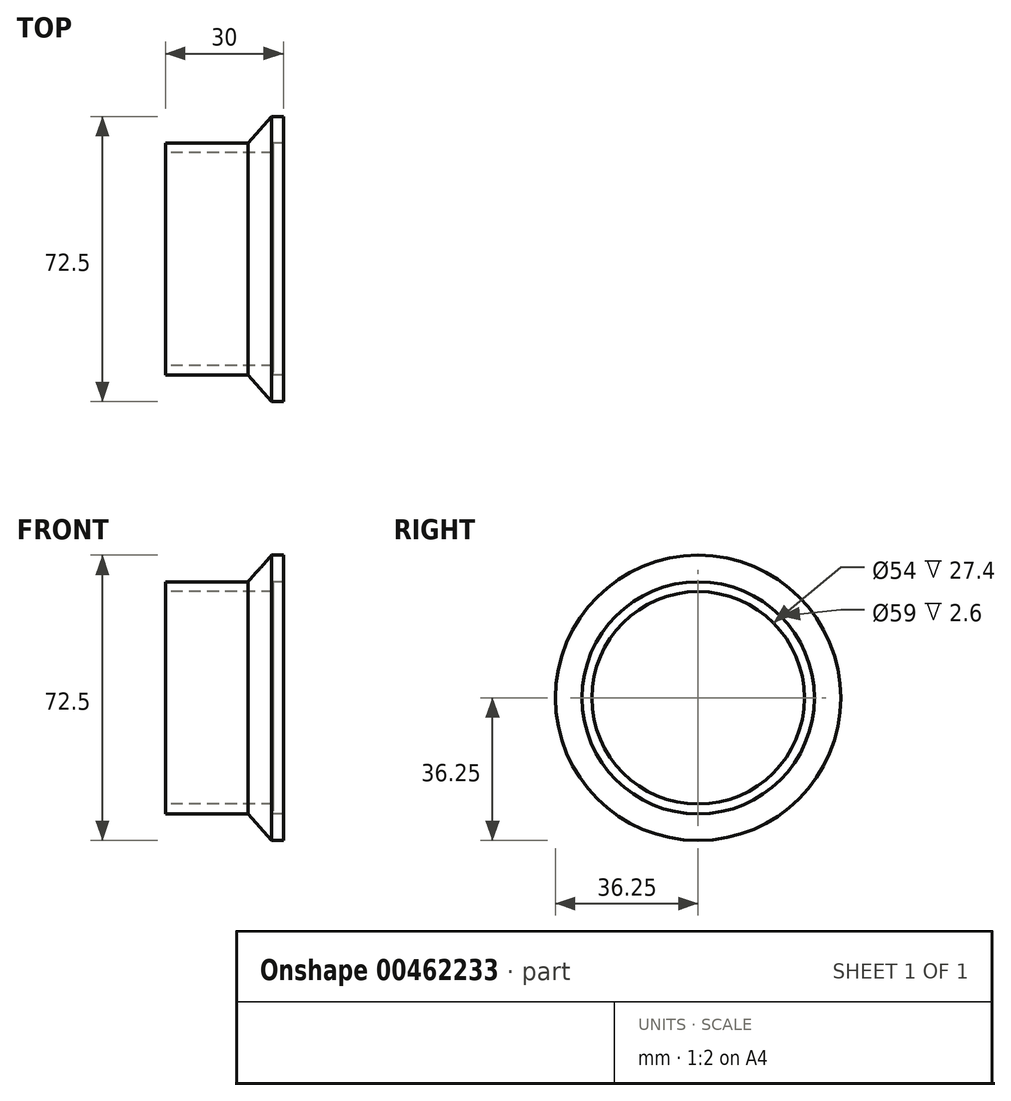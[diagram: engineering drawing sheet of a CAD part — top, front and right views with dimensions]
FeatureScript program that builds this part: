
annotation { "Feature Type Name" : "Feature", "Feature Type Description" : "" }
export const myFeature = defineFeature(function(context is Context, id is Id, definition is map)
    precondition{}
    {
        {
            var Q0;
            Q0=qCreatedBy(makeId("Top.planeOp"),FACE);
            var sketch = newSketch(context, id + "F0", { "sketchPlane" : qUnion([Q0])});
            skLineSegment(sketch, "E0", {"start": v(0, 29.5) * mm, "end": v(21, 29.5) * mm});
            skLineSegment(sketch, "E1", {"start": v(21, 29.5) * mm, "end": v(27, 36.25) * mm});
            skLineSegment(sketch, "E2", {"start": v(27, 36.25) * mm, "end": v(30, 36.25) * mm});
            skLineSegment(sketch, "E3", {"start": v(30, 36.25) * mm, "end": v(30, 29.5) * mm});
            skLineSegment(sketch, "E4", {"start": v(30, 29.5) * mm, "end": v(27.4, 29.5) * mm});
            skLineSegment(sketch, "E5", {"start": v(27.4, 29.5) * mm, "end": v(27.4, 27) * mm});
            skLineSegment(sketch, "E6", {"start": v(27.4, 27) * mm, "end": v(0, 27) * mm});
            skLineSegment(sketch, "E7", {"start": v(0, 27) * mm, "end": v(0, 29.5) * mm});
            skLineSegment(sketch, "E8", {"start": v(-72.9, 0) * mm, "end": v(102.55, 0) * mm});
            skSolve(sketch);
        }
        {
            var Q0;
            Q0 = qSketchRegion(id + "F0", true);
            var Q1;
            Q1=sQuery(id+"F0.wireOp",EDGE,"E8");
            revolve(context, id + "F1", {"entities" : qUnion([Q0]), "axis" : qUnion([Q1]), "revolveType" : RevolveType.FULL});
        }
    });
